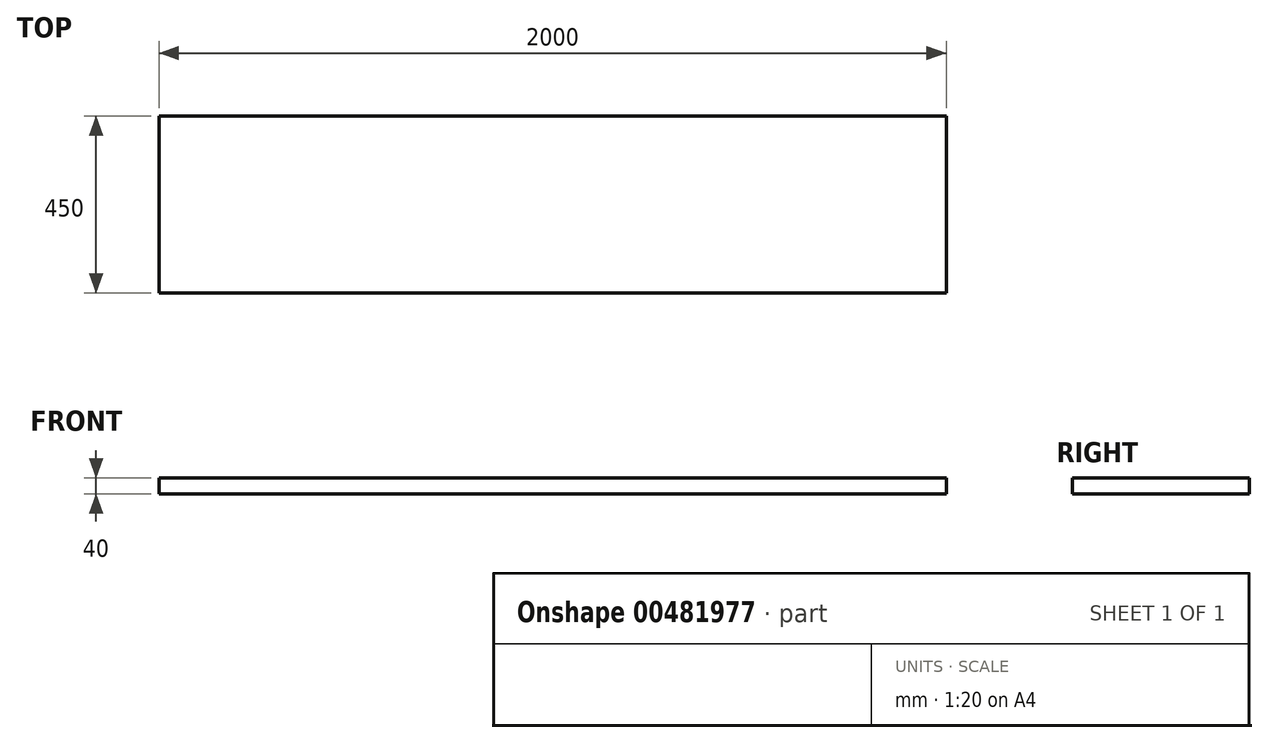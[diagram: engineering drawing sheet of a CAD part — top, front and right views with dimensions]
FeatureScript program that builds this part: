
annotation { "Feature Type Name" : "Feature", "Feature Type Description" : "" }
export const myFeature = defineFeature(function(context is Context, id is Id, definition is map)
    precondition{}
    {
        {
            var Q0;
            Q0=qCreatedBy(makeId("Front.planeOp"),FACE);
            var sketch = newSketch(context, id + "F0", { "sketchPlane" : qUnion([Q0])});
            skLineSegment(sketch, "E0.bottom", {"start": v(-45.38, 25.06) * mm, "end": v(1954.62, 25.06) * mm});
            skLineSegment(sketch, "E0.top", {"start": v(-45.38, 65.06) * mm, "end": v(1954.62, 65.06) * mm});
            skLineSegment(sketch, "E0.left", {"start": v(-45.38, 25.06) * mm, "end": v(-45.38, 65.06) * mm});
            skLineSegment(sketch, "E0.right", {"start": v(1954.62, 25.06) * mm, "end": v(1954.62, 65.06) * mm});
            skSolve(sketch);
        }
        {
            var Q0;
            Q0 = qSketchRegion(id + "F0", true);
            extrude(context, id + "F1", {"entities" : qUnion([Q0]), "depth" : 450 * mm});
        }
    });
